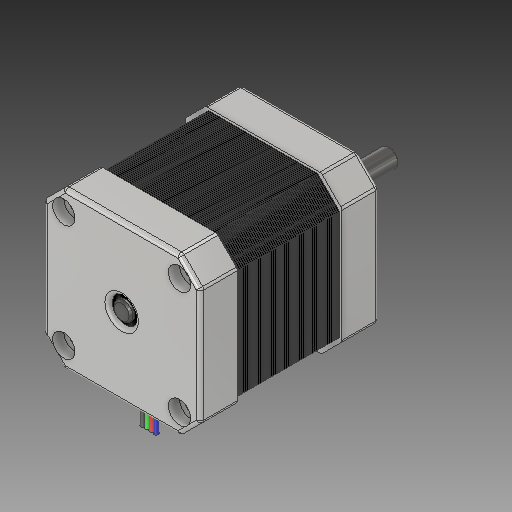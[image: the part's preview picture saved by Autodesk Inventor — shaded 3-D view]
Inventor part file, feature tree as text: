
AUTODESK INVENTOR PART (.ipt)
format: ipt  version: 2018 (Build 220112000, 112)  size: 1,367,552 bytes
history: native  units: mm
features: sketch x5, other x3
ambient origin geometry x8: Origin, YZ Plane, XZ Plane, XY Plane, X Axis, Y Axis, Z Axis, Center Point
bodies: Solid1 (feature_tree)
feature tree (8):
  other  "Nema17.ipt"
  other  "Solid1::Nema17.ipt"
  other  "TaggingFeature1"
  sketch  "Sketch1"  dims[d0=10.0mm]
  sketch  "Sketch4"
  sketch  "Sketch5"
  sketch  "Sketch6"
  sketch  "Sketch11"
